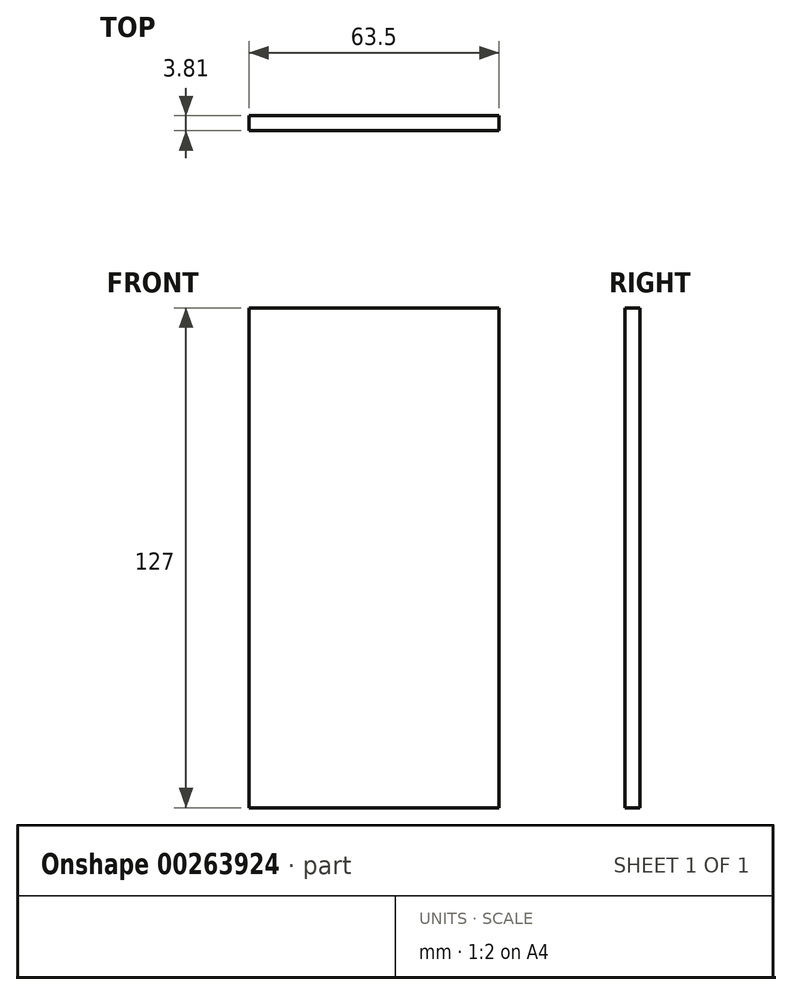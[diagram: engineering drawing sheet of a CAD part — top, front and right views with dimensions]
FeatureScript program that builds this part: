
annotation { "Feature Type Name" : "Feature", "Feature Type Description" : "" }
export const myFeature = defineFeature(function(context is Context, id is Id, definition is map)
    precondition{}
    {
        {
            var Q0;
            Q0=qCreatedBy(makeId("Front.planeOp"),FACE);
            var sketch = newSketch(context, id + "F0", { "sketchPlane" : qUnion([Q0])});
            skLineSegment(sketch, "E0.bottom", {"start": v(31.75, 63.5) * mm, "end": v(-31.75, 63.5) * mm});
            skLineSegment(sketch, "E0.top", {"start": v(31.75, -63.5) * mm, "end": v(-31.75, -63.5) * mm});
            skLineSegment(sketch, "E0.left", {"start": v(31.75, 63.5) * mm, "end": v(31.75, -63.5) * mm});
            skLineSegment(sketch, "E0.right", {"start": v(-31.75, 63.5) * mm, "end": v(-31.75, -63.5) * mm});
            skPoint(sketch, "E0.middle", {"position": v(0, 0) * mm});
            skSolve(sketch);
        }
        {
            var Q0;
            Q0 = qSketchRegion(id + "F0", true);
            extrude(context, id + "F1", {"entities" : qUnion([Q0]), "depth" : 3.8 * mm});
        }
    });
